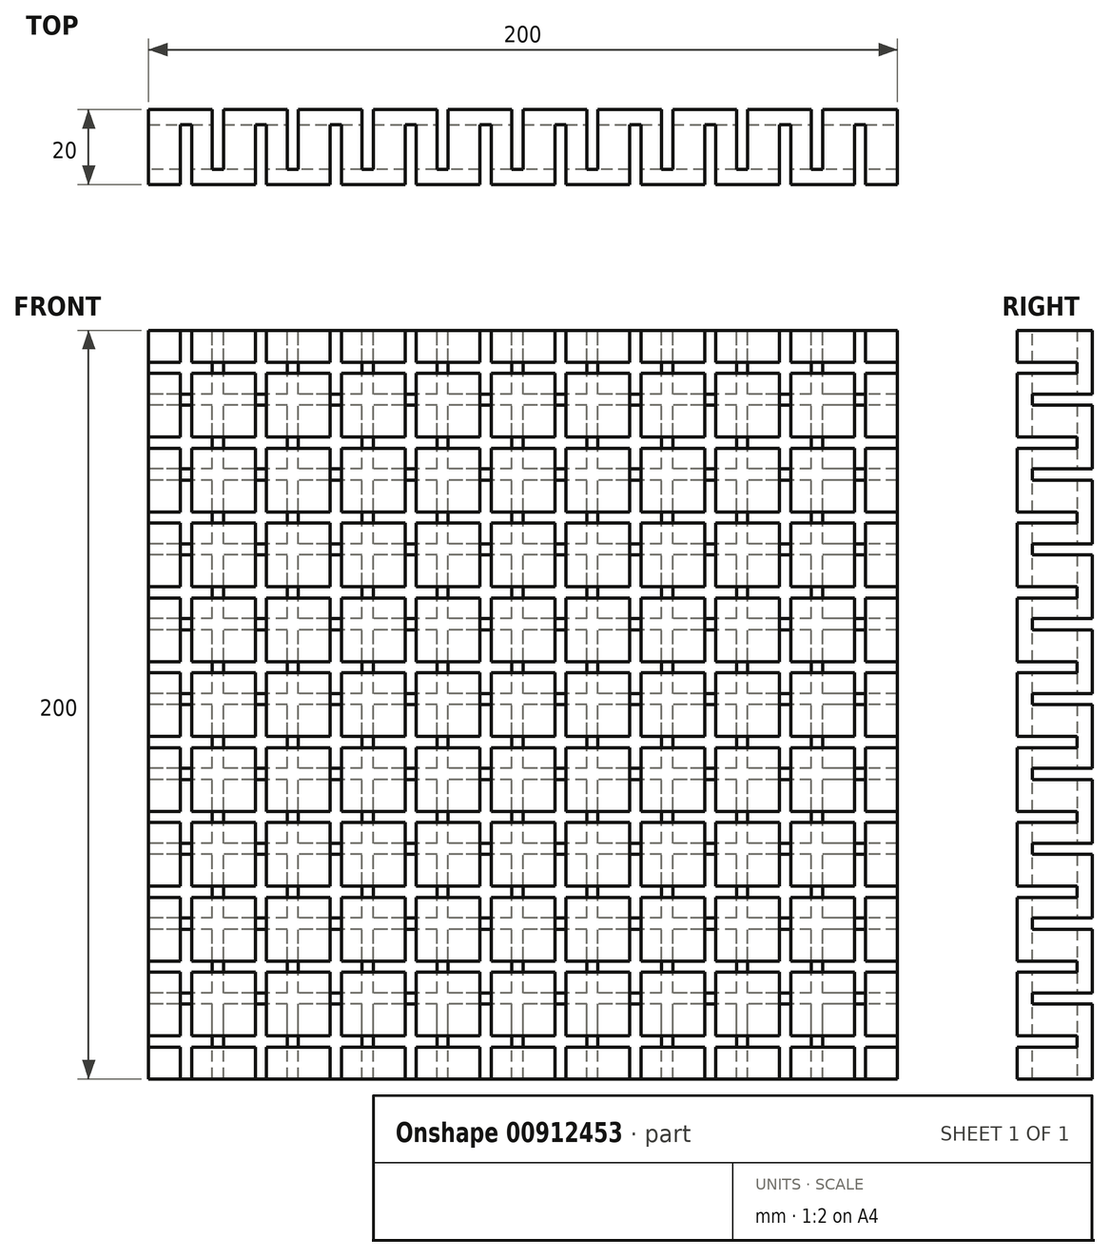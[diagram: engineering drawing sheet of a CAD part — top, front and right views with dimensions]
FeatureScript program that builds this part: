
annotation { "Feature Type Name" : "Feature", "Feature Type Description" : "" }
export const myFeature = defineFeature(function(context is Context, id is Id, definition is map)
    precondition{}
    {
        {
            var Q0;
            Q0=qCreatedBy(makeId("Front.planeOp"),FACE);
            var sketch = newSketch(context, id + "F0", { "sketchPlane" : qUnion([Q0])});
            skLineSegment(sketch, "E0.bottom", {"start": v(100, 100) * mm, "end": v(-100, 100) * mm});
            skLineSegment(sketch, "E0.top", {"start": v(100, -100) * mm, "end": v(-100, -100) * mm});
            skLineSegment(sketch, "E0.left", {"start": v(100, 100) * mm, "end": v(100, -100) * mm});
            skLineSegment(sketch, "E0.right", {"start": v(-100, 100) * mm, "end": v(-100, -100) * mm});
            skPoint(sketch, "E0.middle", {"position": v(0, 0) * mm});
            skSolve(sketch);
        }
        {
            var Q0;
            Q0 = qSketchRegion(id + "F0", true);
            extrude(context, id + "F1", {"entities" : qUnion([Q0]), "depth" : 20 * mm, "offsetDistance" : 25 * mm});
        }
        {
            var Q0;
            Q0=makeQuery(id+"F1.opExtrude","CAP_FACE",FACE,{"disambiguationData":[OSD([sQuery(id+"F0.wireOp",EDGE,"E0.bottom"),sQuery(id+"F0.wireOp",EDGE,"E0.top"),sQuery(id+"F0.wireOp",EDGE,"E0.left"),sQuery(id+"F0.wireOp",EDGE,"E0.right")])],"isStart":false});
            var sketch = newSketch(context, id + "F2", { "sketchPlane" : qUnion([Q0])});
            skLineSegment(sketch, "E1.bottom", {"start": v(-91.5, 100) * mm, "end": v(-88.5, 100) * mm});
            skLineSegment(sketch, "E1.top", {"start": v(-91.5, -100) * mm, "end": v(-88.5, -100) * mm});
            skLineSegment(sketch, "E1.left", {"start": v(-91.5, 100) * mm, "end": v(-91.5, -100) * mm});
            skLineSegment(sketch, "E1.right", {"start": v(-88.5, 100) * mm, "end": v(-88.5, -100) * mm});
            skLineSegment(sketch, "E2.1.0.0", {"start": v(-68.5, 100) * mm, "end": v(-68.5, -100) * mm});
            skLineSegment(sketch, "E2.1.0.1", {"start": v(-71.5, 100) * mm, "end": v(-71.5, -100) * mm});
            skLineSegment(sketch, "E2.1.0.2", {"start": v(-71.5, 100) * mm, "end": v(-68.5, 100) * mm});
            skLineSegment(sketch, "E2.2.0.0", {"start": v(-48.5, 100) * mm, "end": v(-48.5, -100) * mm});
            skLineSegment(sketch, "E2.2.0.1", {"start": v(-51.5, 100) * mm, "end": v(-51.5, -100) * mm});
            skLineSegment(sketch, "E2.2.0.2", {"start": v(-51.5, 100) * mm, "end": v(-48.5, 100) * mm});
            skLineSegment(sketch, "E2.3.0.0", {"start": v(-28.5, 100) * mm, "end": v(-28.5, -100) * mm});
            skLineSegment(sketch, "E2.3.0.1", {"start": v(-31.5, 100) * mm, "end": v(-31.5, -100) * mm});
            skLineSegment(sketch, "E2.3.0.2", {"start": v(-31.5, 100) * mm, "end": v(-28.5, 100) * mm});
            skLineSegment(sketch, "E2.4.0.0", {"start": v(-8.5, 100) * mm, "end": v(-8.5, -100) * mm});
            skLineSegment(sketch, "E2.4.0.1", {"start": v(-11.5, 100) * mm, "end": v(-11.5, -100) * mm});
            skLineSegment(sketch, "E2.4.0.2", {"start": v(-11.5, 100) * mm, "end": v(-8.5, 100) * mm});
            skLineSegment(sketch, "E2.5.0.0", {"start": v(11.5, 100) * mm, "end": v(11.5, -100) * mm});
            skLineSegment(sketch, "E2.5.0.1", {"start": v(8.5, 100) * mm, "end": v(8.5, -100) * mm});
            skLineSegment(sketch, "E2.5.0.2", {"start": v(8.5, 100) * mm, "end": v(11.5, 100) * mm});
            skLineSegment(sketch, "E2.6.0.0", {"start": v(31.5, 100) * mm, "end": v(31.5, -100) * mm});
            skLineSegment(sketch, "E2.6.0.1", {"start": v(28.5, 100) * mm, "end": v(28.5, -100) * mm});
            skLineSegment(sketch, "E2.6.0.2", {"start": v(28.5, 100) * mm, "end": v(31.5, 100) * mm});
            skLineSegment(sketch, "E2.7.0.0", {"start": v(51.5, 100) * mm, "end": v(51.5, -100) * mm});
            skLineSegment(sketch, "E2.7.0.1", {"start": v(48.5, 100) * mm, "end": v(48.5, -100) * mm});
            skLineSegment(sketch, "E2.7.0.2", {"start": v(48.5, 100) * mm, "end": v(51.5, 100) * mm});
            skLineSegment(sketch, "E2.direction1", {"start": v(-88.5, -100) * mm, "end": v(-68.5, -100) * mm, "construction": true});
            skLineSegment(sketch, "E3.0.8.0", {"start": v(71.5, 100) * mm, "end": v(71.5, -100) * mm});
            skLineSegment(sketch, "E3.3.8.0", {"start": v(68.5, 100) * mm, "end": v(68.5, -100) * mm});
            skLineSegment(sketch, "E3.6.8.0", {"start": v(68.5, 100) * mm, "end": v(71.5, 100) * mm});
            skLineSegment(sketch, "E3.0.9.0", {"start": v(91.5, 100) * mm, "end": v(91.5, -100) * mm});
            skLineSegment(sketch, "E3.3.9.0", {"start": v(88.5, 100) * mm, "end": v(88.5, -100) * mm});
            skLineSegment(sketch, "E3.6.9.0", {"start": v(88.5, 100) * mm, "end": v(91.5, 100) * mm});
            skSolve(sketch);
        }
        {
            var Q0;
            Q0 = qSketchRegion(id + "F2", true);
            var Q1;
            {var subQ0=sQuery(id+"F2.wireOp",EDGE,"E2.1.0.0");Q1=makeQuery(id+"F2.imprint","IMPRINT",FACE,{"disambiguationData":[TD([[makeQuery(id+"F2.imprint","IMPRINT",EDGE,{"derivedFrom":subQ0}),-1.0]])]});}
            var Q2;
            {var subQ0=sQuery(id+"F2.wireOp",EDGE,"E2.2.0.0");Q2=makeQuery(id+"F2.imprint","IMPRINT",FACE,{"disambiguationData":[TD([[makeQuery(id+"F2.imprint","IMPRINT",EDGE,{"derivedFrom":subQ0}),-1.0]])]});}
            var Q3;
            {var subQ0=sQuery(id+"F2.wireOp",EDGE,"E2.3.0.0");Q3=makeQuery(id+"F2.imprint","IMPRINT",FACE,{"disambiguationData":[TD([[makeQuery(id+"F2.imprint","IMPRINT",EDGE,{"derivedFrom":subQ0}),-1.0]])]});}
            var Q4;
            {var subQ0=sQuery(id+"F2.wireOp",EDGE,"E2.4.0.0");Q4=makeQuery(id+"F2.imprint","IMPRINT",FACE,{"disambiguationData":[TD([[makeQuery(id+"F2.imprint","IMPRINT",EDGE,{"derivedFrom":subQ0}),-1.0]])]});}
            var Q5;
            {var subQ0=sQuery(id+"F2.wireOp",EDGE,"E2.5.0.0");Q5=makeQuery(id+"F2.imprint","IMPRINT",FACE,{"disambiguationData":[TD([[makeQuery(id+"F2.imprint","IMPRINT",EDGE,{"derivedFrom":subQ0}),-1.0]])]});}
            var Q6;
            {var subQ0=sQuery(id+"F2.wireOp",EDGE,"E2.6.0.0");Q6=makeQuery(id+"F2.imprint","IMPRINT",FACE,{"disambiguationData":[TD([[makeQuery(id+"F2.imprint","IMPRINT",EDGE,{"derivedFrom":subQ0}),-1.0]])]});}
            var Q7;
            {var subQ0=sQuery(id+"F2.wireOp",EDGE,"E2.7.0.0");Q7=makeQuery(id+"F2.imprint","IMPRINT",FACE,{"disambiguationData":[TD([[makeQuery(id+"F2.imprint","IMPRINT",EDGE,{"derivedFrom":subQ0}),-1.0]])]});}
            var Q8;
            {var subQ0=sQuery(id+"F2.wireOp",EDGE,"E3.0.8.0");Q8=makeQuery(id+"F2.imprint","IMPRINT",FACE,{"disambiguationData":[TD([[makeQuery(id+"F2.imprint","IMPRINT",EDGE,{"derivedFrom":subQ0}),-1.0]])]});}
            var Q9;
            {var subQ0=sQuery(id+"F2.wireOp",EDGE,"E3.0.9.0");Q9=makeQuery(id+"F2.imprint","IMPRINT",FACE,{"disambiguationData":[TD([[makeQuery(id+"F2.imprint","IMPRINT",EDGE,{"derivedFrom":subQ0}),-1.0]])]});}
            extrude(context, id + "F3", {"entities" : qUnion([Q0, Q1, Q2, Q3, Q4, Q5, Q6, Q7, Q8, Q9]), "operationType" : NewBodyOperationType.REMOVE, "oppositeDirection" : true, "depth" : 16 * mm, "offsetDistance" : 25 * mm});
        }
        {
            var Q0;
            Q0=makeQuery(id+"F1.opExtrude","CAP_FACE",FACE,{"disambiguationData":[OSD([sQuery(id+"F0.wireOp",EDGE,"E0.bottom"),sQuery(id+"F0.wireOp",EDGE,"E0.top"),sQuery(id+"F0.wireOp",EDGE,"E0.left"),sQuery(id+"F0.wireOp",EDGE,"E0.right")])],"isStart":true});
            var sketch = newSketch(context, id + "F4", { "sketchPlane" : qUnion([Q0])});
            skLineSegment(sketch, "E4.bottom", {"start": v(83, -100) * mm, "end": v(80, -100) * mm});
            skLineSegment(sketch, "E4.top", {"start": v(83, 100) * mm, "end": v(80, 100) * mm});
            skLineSegment(sketch, "E4.left", {"start": v(83, -100) * mm, "end": v(83, 100) * mm});
            skLineSegment(sketch, "E4.right", {"start": v(80, -100) * mm, "end": v(80, 100) * mm});
            skLineSegment(sketch, "E5.1.0.0", {"start": v(63, -100) * mm, "end": v(63, 100) * mm});
            skLineSegment(sketch, "E5.1.0.1", {"start": v(63, 100) * mm, "end": v(60, 100) * mm});
            skLineSegment(sketch, "E5.1.0.2", {"start": v(60, -100) * mm, "end": v(60, 100) * mm});
            skLineSegment(sketch, "E5.1.0.3", {"start": v(63, -100) * mm, "end": v(60, -100) * mm});
            skLineSegment(sketch, "E5.2.0.0", {"start": v(43, -100) * mm, "end": v(43, 100) * mm});
            skLineSegment(sketch, "E5.2.0.1", {"start": v(43, 100) * mm, "end": v(40, 100) * mm});
            skLineSegment(sketch, "E5.2.0.2", {"start": v(40, -100) * mm, "end": v(40, 100) * mm});
            skLineSegment(sketch, "E5.2.0.3", {"start": v(43, -100) * mm, "end": v(40, -100) * mm});
            skLineSegment(sketch, "E5.3.0.0", {"start": v(23, -100) * mm, "end": v(23, 100) * mm});
            skLineSegment(sketch, "E5.3.0.1", {"start": v(23, 100) * mm, "end": v(20, 100) * mm});
            skLineSegment(sketch, "E5.3.0.2", {"start": v(20, -100) * mm, "end": v(20, 100) * mm});
            skLineSegment(sketch, "E5.3.0.3", {"start": v(23, -100) * mm, "end": v(20, -100) * mm});
            skLineSegment(sketch, "E5.4.0.0", {"start": v(3, -100) * mm, "end": v(3, 100) * mm});
            skLineSegment(sketch, "E5.4.0.1", {"start": v(3, 100) * mm, "end": v(0, 100) * mm});
            skLineSegment(sketch, "E5.4.0.2", {"start": v(0, -100) * mm, "end": v(0, 100) * mm});
            skLineSegment(sketch, "E5.4.0.3", {"start": v(3, -100) * mm, "end": v(0, -100) * mm});
            skLineSegment(sketch, "E5.5.0.0", {"start": v(-17, -100) * mm, "end": v(-17, 100) * mm});
            skLineSegment(sketch, "E5.5.0.1", {"start": v(-17, 100) * mm, "end": v(-20, 100) * mm});
            skLineSegment(sketch, "E5.5.0.2", {"start": v(-20, -100) * mm, "end": v(-20, 100) * mm});
            skLineSegment(sketch, "E5.5.0.3", {"start": v(-17, -100) * mm, "end": v(-20, -100) * mm});
            skLineSegment(sketch, "E5.6.0.0", {"start": v(-37, -100) * mm, "end": v(-37, 100) * mm});
            skLineSegment(sketch, "E5.6.0.1", {"start": v(-37, 100) * mm, "end": v(-40, 100) * mm});
            skLineSegment(sketch, "E5.6.0.2", {"start": v(-40, -100) * mm, "end": v(-40, 100) * mm});
            skLineSegment(sketch, "E5.6.0.3", {"start": v(-37, -100) * mm, "end": v(-40, -100) * mm});
            skLineSegment(sketch, "E5.7.0.0", {"start": v(-57, -100) * mm, "end": v(-57, 100) * mm});
            skLineSegment(sketch, "E5.7.0.1", {"start": v(-57, 100) * mm, "end": v(-60, 100) * mm});
            skLineSegment(sketch, "E5.7.0.2", {"start": v(-60, -100) * mm, "end": v(-60, 100) * mm});
            skLineSegment(sketch, "E5.7.0.3", {"start": v(-57, -100) * mm, "end": v(-60, -100) * mm});
            skLineSegment(sketch, "E5.8.0.0", {"start": v(-77, -100) * mm, "end": v(-77, 100) * mm});
            skLineSegment(sketch, "E5.8.0.1", {"start": v(-77, 100) * mm, "end": v(-80, 100) * mm});
            skLineSegment(sketch, "E5.8.0.2", {"start": v(-80, -100) * mm, "end": v(-80, 100) * mm});
            skLineSegment(sketch, "E5.8.0.3", {"start": v(-77, -100) * mm, "end": v(-80, -100) * mm});
            skLineSegment(sketch, "E5.direction1", {"start": v(83, -100) * mm, "end": v(63, -100) * mm, "construction": true});
            skSolve(sketch);
        }
        {
            var Q0;
            Q0=makeQuery(id+"F4.imprint","IMPRINT",FACE,{"disambiguationData":[TD([[makeQuery(id+"F4.imprint","IMPRINT",EDGE,{"derivedFrom":sQuery(id+"F4.wireOp",EDGE,"E5.7.0.0")}),1.0]])]});
            var Q1;
            Q1=makeQuery(id+"F4.imprint","IMPRINT",FACE,{"disambiguationData":[TD([[makeQuery(id+"F4.imprint","IMPRINT",EDGE,{"derivedFrom":sQuery(id+"F4.wireOp",EDGE,"E5.6.0.0")}),1.0]])]});
            var Q2;
            Q2=makeQuery(id+"F4.imprint","IMPRINT",FACE,{"disambiguationData":[TD([[makeQuery(id+"F4.imprint","IMPRINT",EDGE,{"derivedFrom":sQuery(id+"F4.wireOp",EDGE,"E5.5.0.0")}),1.0]])]});
            var Q3;
            Q3=makeQuery(id+"F4.imprint","IMPRINT",FACE,{"disambiguationData":[TD([[makeQuery(id+"F4.imprint","IMPRINT",EDGE,{"derivedFrom":sQuery(id+"F4.wireOp",EDGE,"E5.4.0.0")}),1.0]])]});
            var Q4;
            Q4=makeQuery(id+"F4.imprint","IMPRINT",FACE,{"disambiguationData":[TD([[makeQuery(id+"F4.imprint","IMPRINT",EDGE,{"derivedFrom":sQuery(id+"F4.wireOp",EDGE,"E5.3.0.0")}),1.0]])]});
            var Q5;
            Q5=makeQuery(id+"F4.imprint","IMPRINT",FACE,{"disambiguationData":[TD([[makeQuery(id+"F4.imprint","IMPRINT",EDGE,{"derivedFrom":sQuery(id+"F4.wireOp",EDGE,"E5.2.0.0")}),1.0]])]});
            var Q6;
            Q6=makeQuery(id+"F4.imprint","IMPRINT",FACE,{"disambiguationData":[TD([[makeQuery(id+"F4.imprint","IMPRINT",EDGE,{"derivedFrom":sQuery(id+"F4.wireOp",EDGE,"E5.1.0.0")}),1.0]])]});
            var Q7;
            Q7=makeQuery(id+"F4.imprint","IMPRINT",FACE,{"disambiguationData":[TD([[makeQuery(id+"F4.imprint","IMPRINT",EDGE,{"derivedFrom":sQuery(id+"F4.wireOp",EDGE,"E4.bottom")}),1.0]])]});
            var Q8;
            Q8=makeQuery(id+"F4.imprint","IMPRINT",FACE,{"disambiguationData":[TD([[makeQuery(id+"F4.imprint","IMPRINT",EDGE,{"derivedFrom":sQuery(id+"F4.wireOp",EDGE,"E5.8.0.0")}),1.0]])]});
            extrude(context, id + "F5", {"entities" : qUnion([Q0, Q1, Q2, Q3, Q4, Q5, Q6, Q7, Q8]), "operationType" : NewBodyOperationType.REMOVE, "oppositeDirection" : true, "depth" : 16 * mm, "offsetDistance" : 25 * mm});
        }
        {
            var Q0;
            Q0=qCreatedBy(makeId("Front.planeOp"),FACE);
            cPlane(context, id + "F6", {"entities" : qUnion([Q0]), "cplaneType" : CPlaneType.OFFSET, "offset" : 20 * mm, "width" : 150 * mm, "height" : 150 * mm});
        }
        {
            var Q0;
            Q0=qCreatedBy(id+"F6.planeOp",FACE);
            var sketch = newSketch(context, id + "F7", { "sketchPlane" : qUnion([Q0])});
            skLineSegment(sketch, "E6.bottom", {"start": v(100, -100) * mm, "end": v(-100, -100) * mm, "construction": true});
            skLineSegment(sketch, "E6.top", {"start": v(100, 100) * mm, "end": v(-100, 100) * mm, "construction": true});
            skPoint(sketch, "E6.middle", {"position": v(0, 0) * mm});
            skLineSegment(sketch, "E7.bottom", {"start": v(-100, 91.5) * mm, "end": v(100, 91.5) * mm});
            skLineSegment(sketch, "E7.top", {"start": v(-100, 88.5) * mm, "end": v(100, 88.5) * mm});
            skLineSegment(sketch, "E7.left", {"start": v(-100, 91.5) * mm, "end": v(-100, 88.5) * mm});
            skLineSegment(sketch, "E7.right", {"start": v(100, 91.5) * mm, "end": v(100, 88.5) * mm});
            skLineSegment(sketch, "E8.0.1.0", {"start": v(-100, 71.5) * mm, "end": v(-100, 68.5) * mm});
            skLineSegment(sketch, "E8.0.1.1", {"start": v(-100, 71.5) * mm, "end": v(100, 71.5) * mm});
            skLineSegment(sketch, "E8.0.1.2", {"start": v(-100, 68.5) * mm, "end": v(100, 68.5) * mm});
            skLineSegment(sketch, "E8.0.1.3", {"start": v(100, 71.5) * mm, "end": v(100, 68.5) * mm});
            skLineSegment(sketch, "E8.0.2.0", {"start": v(-100, 51.5) * mm, "end": v(-100, 48.5) * mm});
            skLineSegment(sketch, "E8.0.2.1", {"start": v(-100, 51.5) * mm, "end": v(100, 51.5) * mm});
            skLineSegment(sketch, "E8.0.2.2", {"start": v(-100, 48.5) * mm, "end": v(100, 48.5) * mm});
            skLineSegment(sketch, "E8.0.2.3", {"start": v(100, 51.5) * mm, "end": v(100, 48.5) * mm});
            skLineSegment(sketch, "E8.0.3.0", {"start": v(-100, 31.5) * mm, "end": v(-100, 28.5) * mm});
            skLineSegment(sketch, "E8.0.3.1", {"start": v(-100, 31.5) * mm, "end": v(100, 31.5) * mm});
            skLineSegment(sketch, "E8.0.3.2", {"start": v(-100, 28.5) * mm, "end": v(100, 28.5) * mm});
            skLineSegment(sketch, "E8.0.3.3", {"start": v(100, 31.5) * mm, "end": v(100, 28.5) * mm});
            skLineSegment(sketch, "E8.0.4.0", {"start": v(-100, 11.5) * mm, "end": v(-100, 8.5) * mm});
            skLineSegment(sketch, "E8.0.4.1", {"start": v(-100, 11.5) * mm, "end": v(100, 11.5) * mm});
            skLineSegment(sketch, "E8.0.4.2", {"start": v(-100, 8.5) * mm, "end": v(100, 8.5) * mm});
            skLineSegment(sketch, "E8.0.4.3", {"start": v(100, 11.5) * mm, "end": v(100, 8.5) * mm});
            skLineSegment(sketch, "E8.0.5.0", {"start": v(-100, -8.5) * mm, "end": v(-100, -11.5) * mm});
            skLineSegment(sketch, "E8.0.5.1", {"start": v(-100, -8.5) * mm, "end": v(100, -8.5) * mm});
            skLineSegment(sketch, "E8.0.5.2", {"start": v(-100, -11.5) * mm, "end": v(100, -11.5) * mm});
            skLineSegment(sketch, "E8.0.5.3", {"start": v(100, -8.5) * mm, "end": v(100, -11.5) * mm});
            skLineSegment(sketch, "E8.0.6.0", {"start": v(-100, -28.5) * mm, "end": v(-100, -31.5) * mm});
            skLineSegment(sketch, "E8.0.6.1", {"start": v(-100, -28.5) * mm, "end": v(100, -28.5) * mm});
            skLineSegment(sketch, "E8.0.6.2", {"start": v(-100, -31.5) * mm, "end": v(100, -31.5) * mm});
            skLineSegment(sketch, "E8.0.6.3", {"start": v(100, -28.5) * mm, "end": v(100, -31.5) * mm});
            skLineSegment(sketch, "E8.0.7.0", {"start": v(-100, -48.5) * mm, "end": v(-100, -51.5) * mm});
            skLineSegment(sketch, "E8.0.7.1", {"start": v(-100, -48.5) * mm, "end": v(100, -48.5) * mm});
            skLineSegment(sketch, "E8.0.7.2", {"start": v(-100, -51.5) * mm, "end": v(100, -51.5) * mm});
            skLineSegment(sketch, "E8.0.7.3", {"start": v(100, -48.5) * mm, "end": v(100, -51.5) * mm});
            skLineSegment(sketch, "E8.0.8.0", {"start": v(-100, -68.5) * mm, "end": v(-100, -71.5) * mm});
            skLineSegment(sketch, "E8.0.8.1", {"start": v(-100, -68.5) * mm, "end": v(100, -68.5) * mm});
            skLineSegment(sketch, "E8.0.8.2", {"start": v(-100, -71.5) * mm, "end": v(100, -71.5) * mm});
            skLineSegment(sketch, "E8.0.8.3", {"start": v(100, -68.5) * mm, "end": v(100, -71.5) * mm});
            skLineSegment(sketch, "E8.0.9.0", {"start": v(-100, -88.5) * mm, "end": v(-100, -91.5) * mm});
            skLineSegment(sketch, "E8.0.9.1", {"start": v(-100, -88.5) * mm, "end": v(100, -88.5) * mm});
            skLineSegment(sketch, "E8.0.9.2", {"start": v(-100, -91.5) * mm, "end": v(100, -91.5) * mm});
            skLineSegment(sketch, "E8.0.9.3", {"start": v(100, -88.5) * mm, "end": v(100, -91.5) * mm});
            skLineSegment(sketch, "E8.direction1", {"start": v(-100, 88.5) * mm, "end": v(-75, 88.5) * mm, "construction": true});
            skLineSegment(sketch, "E8.direction2", {"start": v(-100, 88.5) * mm, "end": v(-100, 68.5) * mm, "construction": true});
            skSolve(sketch);
        }
        {
            var Q0;
            Q0 = qSketchRegion(id + "F7", true);
            extrude(context, id + "F8", {"entities" : qUnion([Q0]), "operationType" : NewBodyOperationType.REMOVE, "oppositeDirection" : true, "depth" : 16 * mm, "offsetDistance" : 25 * mm});
        }
        {
            var Q0;
            Q0=qCreatedBy(makeId("Front.planeOp"),FACE);
            var sketch = newSketch(context, id + "F9", { "sketchPlane" : qUnion([Q0])});
            skLineSegment(sketch, "E9.bottom", {"start": v(100, 100) * mm, "end": v(-100, 100) * mm, "construction": true});
            skLineSegment(sketch, "E9.top", {"start": v(100, -100) * mm, "end": v(-100, -100) * mm, "construction": true});
            skLineSegment(sketch, "E10.bottom", {"start": v(100, 83) * mm, "end": v(-100, 83) * mm});
            skLineSegment(sketch, "E10.top", {"start": v(100, 80) * mm, "end": v(-100, 80) * mm});
            skLineSegment(sketch, "E10.left", {"start": v(100, 83) * mm, "end": v(100, 80) * mm});
            skLineSegment(sketch, "E10.right", {"start": v(-100, 83) * mm, "end": v(-100, 80) * mm});
            skLineSegment(sketch, "E11.0.1.0", {"start": v(100, 63) * mm, "end": v(-100, 63) * mm});
            skLineSegment(sketch, "E11.0.1.1", {"start": v(100, 60) * mm, "end": v(-100, 60) * mm});
            skLineSegment(sketch, "E11.0.1.2", {"start": v(100, 63) * mm, "end": v(100, 60) * mm});
            skLineSegment(sketch, "E11.0.1.3", {"start": v(-100, 63) * mm, "end": v(-100, 60) * mm});
            skLineSegment(sketch, "E11.0.2.0", {"start": v(100, 43) * mm, "end": v(-100, 43) * mm});
            skLineSegment(sketch, "E11.0.2.1", {"start": v(100, 40) * mm, "end": v(-100, 40) * mm});
            skLineSegment(sketch, "E11.0.2.2", {"start": v(100, 43) * mm, "end": v(100, 40) * mm});
            skLineSegment(sketch, "E11.0.2.3", {"start": v(-100, 43) * mm, "end": v(-100, 40) * mm});
            skLineSegment(sketch, "E11.0.3.0", {"start": v(100, 23) * mm, "end": v(-100, 23) * mm});
            skLineSegment(sketch, "E11.0.3.1", {"start": v(100, 20) * mm, "end": v(-100, 20) * mm});
            skLineSegment(sketch, "E11.0.3.2", {"start": v(100, 23) * mm, "end": v(100, 20) * mm});
            skLineSegment(sketch, "E11.0.3.3", {"start": v(-100, 23) * mm, "end": v(-100, 20) * mm});
            skLineSegment(sketch, "E11.0.4.0", {"start": v(100, 3) * mm, "end": v(-100, 3) * mm});
            skLineSegment(sketch, "E11.0.4.1", {"start": v(100, 0) * mm, "end": v(-100, 0) * mm});
            skLineSegment(sketch, "E11.0.4.2", {"start": v(100, 3) * mm, "end": v(100, 0) * mm});
            skLineSegment(sketch, "E11.0.4.3", {"start": v(-100, 3) * mm, "end": v(-100, 0) * mm});
            skLineSegment(sketch, "E11.0.5.0", {"start": v(100, -17) * mm, "end": v(-100, -17) * mm});
            skLineSegment(sketch, "E11.0.5.1", {"start": v(100, -20) * mm, "end": v(-100, -20) * mm});
            skLineSegment(sketch, "E11.0.5.2", {"start": v(100, -17) * mm, "end": v(100, -20) * mm});
            skLineSegment(sketch, "E11.0.5.3", {"start": v(-100, -17) * mm, "end": v(-100, -20) * mm});
            skLineSegment(sketch, "E11.0.6.0", {"start": v(100, -37) * mm, "end": v(-100, -37) * mm});
            skLineSegment(sketch, "E11.0.6.1", {"start": v(100, -40) * mm, "end": v(-100, -40) * mm});
            skLineSegment(sketch, "E11.0.6.2", {"start": v(100, -37) * mm, "end": v(100, -40) * mm});
            skLineSegment(sketch, "E11.0.6.3", {"start": v(-100, -37) * mm, "end": v(-100, -40) * mm});
            skLineSegment(sketch, "E11.0.7.0", {"start": v(100, -57) * mm, "end": v(-100, -57) * mm});
            skLineSegment(sketch, "E11.0.7.1", {"start": v(100, -60) * mm, "end": v(-100, -60) * mm});
            skLineSegment(sketch, "E11.0.7.2", {"start": v(100, -57) * mm, "end": v(100, -60) * mm});
            skLineSegment(sketch, "E11.0.7.3", {"start": v(-100, -57) * mm, "end": v(-100, -60) * mm});
            skLineSegment(sketch, "E11.0.8.0", {"start": v(100, -77) * mm, "end": v(-100, -77) * mm});
            skLineSegment(sketch, "E11.0.8.1", {"start": v(100, -80) * mm, "end": v(-100, -80) * mm});
            skLineSegment(sketch, "E11.0.8.2", {"start": v(100, -77) * mm, "end": v(100, -80) * mm});
            skLineSegment(sketch, "E11.0.8.3", {"start": v(-100, -77) * mm, "end": v(-100, -80) * mm});
            skLineSegment(sketch, "E11.direction1", {"start": v(-100, 83) * mm, "end": v(-75, 83) * mm, "construction": true});
            skLineSegment(sketch, "E11.direction2", {"start": v(-100, 83) * mm, "end": v(-100, 63) * mm, "construction": true});
            skSolve(sketch);
        }
        {
            var Q0;
            Q0 = qSketchRegion(id + "F9", true);
            var Q1;
            Q1=sQuery(id+"F9.wireOp",EDGE,"E10.bottom");
            var Q2;
            Q2=sQuery(id+"F9.wireOp",EDGE,"E10.left");
            var Q3;
            Q3=sQuery(id+"F9.wireOp",EDGE,"E10.right");
            var Q4;
            Q4=sQuery(id+"F9.wireOp",EDGE,"E11.0.1.0");
            var Q5;
            Q5=sQuery(id+"F9.wireOp",EDGE,"E11.0.1.1");
            var Q6;
            Q6=sQuery(id+"F9.wireOp",EDGE,"E11.0.1.2");
            var Q7;
            Q7=sQuery(id+"F9.wireOp",EDGE,"E11.0.1.3");
            var Q8;
            Q8=sQuery(id+"F9.wireOp",EDGE,"E11.0.2.0");
            var Q9;
            Q9=sQuery(id+"F9.wireOp",EDGE,"E11.0.2.1");
            var Q10;
            Q10=sQuery(id+"F9.wireOp",EDGE,"E11.0.2.2");
            var Q11;
            Q11=sQuery(id+"F9.wireOp",EDGE,"E11.0.2.3");
            var Q12;
            Q12=sQuery(id+"F9.wireOp",EDGE,"E11.0.3.0");
            var Q13;
            Q13=sQuery(id+"F9.wireOp",EDGE,"E11.0.3.1");
            var Q14;
            Q14=sQuery(id+"F9.wireOp",EDGE,"E11.0.3.2");
            var Q15;
            Q15=sQuery(id+"F9.wireOp",EDGE,"E11.0.3.3");
            var Q16;
            Q16=sQuery(id+"F9.wireOp",EDGE,"E11.0.4.0");
            var Q17;
            Q17=sQuery(id+"F9.wireOp",EDGE,"E11.0.4.1");
            var Q18;
            Q18=sQuery(id+"F9.wireOp",EDGE,"E11.0.4.2");
            var Q19;
            Q19=sQuery(id+"F9.wireOp",EDGE,"E11.0.4.3");
            var Q20;
            Q20=sQuery(id+"F9.wireOp",EDGE,"E11.0.5.0");
            var Q21;
            Q21=sQuery(id+"F9.wireOp",EDGE,"E11.0.5.1");
            var Q22;
            Q22=sQuery(id+"F9.wireOp",EDGE,"E11.0.5.2");
            var Q23;
            Q23=sQuery(id+"F9.wireOp",EDGE,"E11.0.5.3");
            var Q24;
            Q24=sQuery(id+"F9.wireOp",EDGE,"E11.0.6.0");
            var Q25;
            Q25=sQuery(id+"F9.wireOp",EDGE,"E11.0.6.1");
            var Q26;
            Q26=sQuery(id+"F9.wireOp",EDGE,"E11.0.6.2");
            var Q27;
            Q27=sQuery(id+"F9.wireOp",EDGE,"E11.0.6.3");
            var Q28;
            Q28=sQuery(id+"F9.wireOp",EDGE,"E11.0.7.0");
            var Q29;
            Q29=sQuery(id+"F9.wireOp",EDGE,"E11.0.7.1");
            var Q30;
            Q30=sQuery(id+"F9.wireOp",EDGE,"E11.0.7.2");
            var Q31;
            Q31=sQuery(id+"F9.wireOp",EDGE,"E11.0.7.3");
            var Q32;
            Q32=sQuery(id+"F9.wireOp",EDGE,"E11.0.8.0");
            var Q33;
            Q33=sQuery(id+"F9.wireOp",EDGE,"E11.0.8.1");
            var Q34;
            Q34=sQuery(id+"F9.wireOp",EDGE,"E11.0.8.2");
            var Q35;
            Q35=sQuery(id+"F9.wireOp",EDGE,"E11.0.8.3");
            var Q36;
            Q36=sQuery(id+"F9.wireOp",EDGE,"E10.top");
            extrude(context, id + "F10", {"entities" : qUnion([Q0]), "operationType" : NewBodyOperationType.REMOVE, "surfaceEntities" : qUnion([Q1, Q2, Q3, Q4, Q5, Q6, Q7, Q8, Q9, Q10, Q11, Q12, Q13, Q14, Q15, Q16, Q17, Q18, Q19, Q20, Q21, Q22, Q23, Q24, Q25, Q26, Q27, Q28, Q29, Q30, Q31, Q32, Q33, Q34, Q35, Q36]), "depth" : 16 * mm, "offsetDistance" : 25 * mm});
        }
    });
